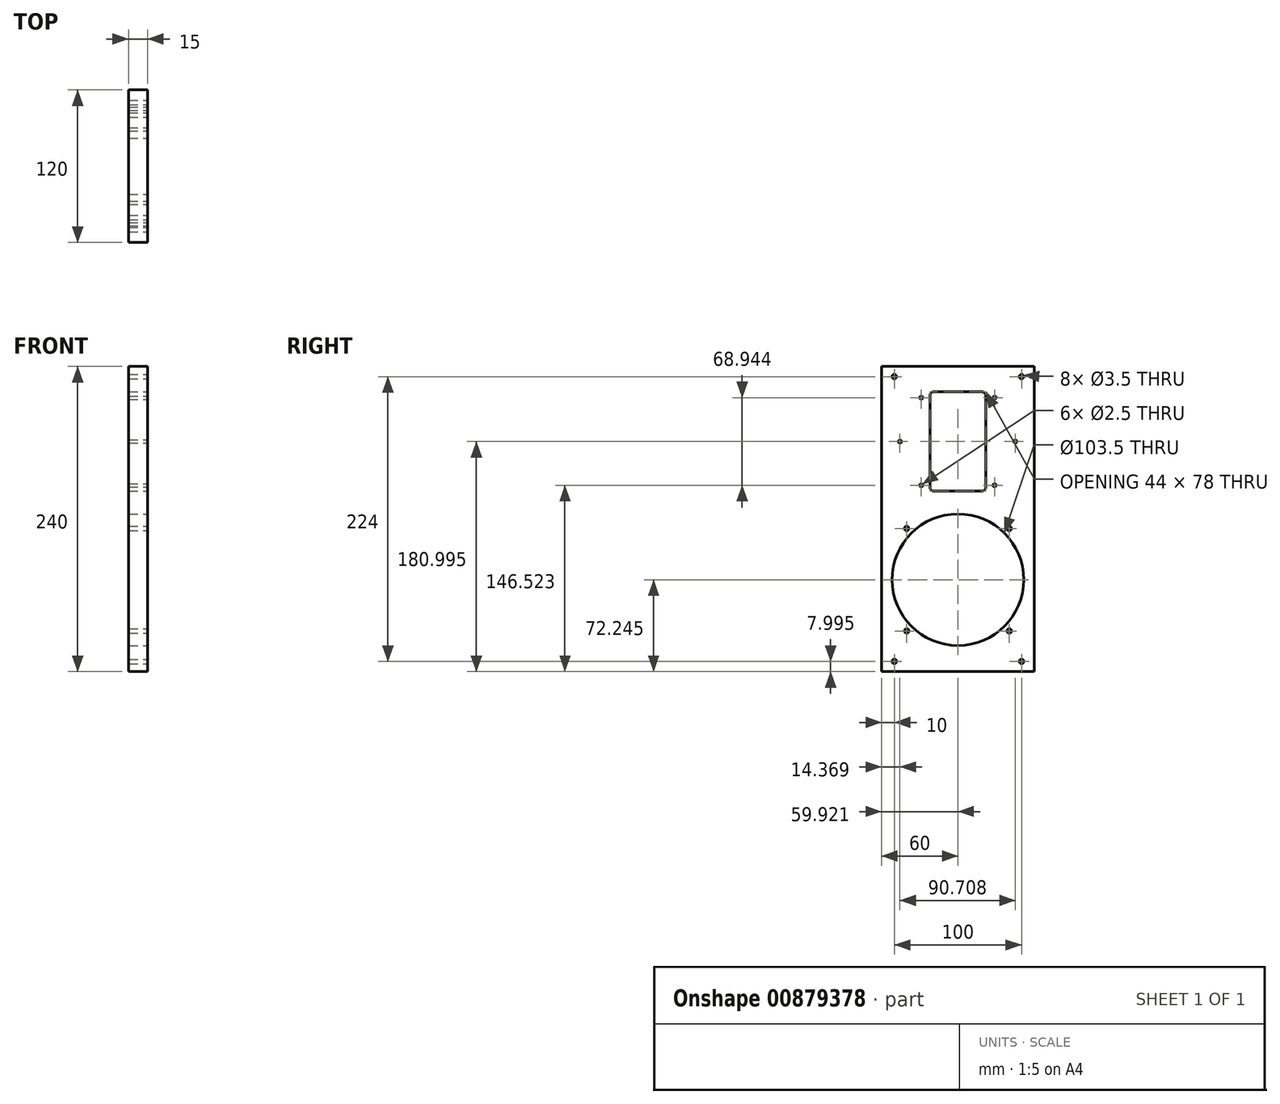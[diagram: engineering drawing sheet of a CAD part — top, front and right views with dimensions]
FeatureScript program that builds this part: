
annotation { "Feature Type Name" : "Feature", "Feature Type Description" : "" }
export const myFeature = defineFeature(function(context is Context, id is Id, definition is map)
    precondition{}
    {
        {
            var Q0;
            Q0=qCreatedBy(makeId("Right.planeOp"),FACE);
            var sketch = newSketch(context, id + "F0", { "sketchPlane" : qUnion([Q0])});
            skLineSegment(sketch, "E0.bottom", {"start": v(60, 124.94) * mm, "end": v(-60, 124.94) * mm});
            skLineSegment(sketch, "E1", {"start": v(60, -115.06) * mm, "end": v(-60, -115.06) * mm});
            skPoint(sketch, "E2", {"position": v(0, -42.81) * mm});
            skCircle(sketch, "E3", {"center": v(0, -42.81) * mm, "radius": 51.75 * mm});
            skCircle(sketch, "E4", {"center": v(40.3, -2.5) * mm, "radius": 1.75 * mm});
            skPoint(sketch, "E5", {"position": v(46.32, 3.5) * mm});
            skPoint(sketch, "E6", {"position": v(47.02, 4.2) * mm});
            skCircle(sketch, "E7.1.0", {"center": v(-40.3, -2.5) * mm, "radius": 1.75 * mm});
            skPoint(sketch, "E7.1.1", {"position": v(-46.32, 3.5) * mm});
            skPoint(sketch, "E7.1.2", {"position": v(-47.02, 4.2) * mm});
            skCircle(sketch, "E7.2.0", {"center": v(-40.3, -83.12) * mm, "radius": 1.75 * mm});
            skPoint(sketch, "E7.2.1", {"position": v(-46.32, -89.13) * mm});
            skPoint(sketch, "E7.2.2", {"position": v(-47.02, -89.84) * mm});
            skCircle(sketch, "E7.3.0", {"center": v(40.3, -83.12) * mm, "radius": 1.75 * mm});
            skPoint(sketch, "E7.3.1", {"position": v(46.32, -89.13) * mm});
            skPoint(sketch, "E7.3.2", {"position": v(47.02, -89.84) * mm});
            skPoint(sketch, "E8.1.0", {"position": v(-57, -42.81) * mm});
            skPoint(sketch, "E8.2.0", {"position": v(0, -99.81) * mm});
            skPoint(sketch, "E8.3.0", {"position": v(57, -42.81) * mm});
            skLineSegment(sketch, "E9.trimOffspring", {"start": v(0, 15.94) * mm, "end": v(0, 15.98) * mm});
            skLineSegment(sketch, "E10.trimOffspring", {"start": v(46.32, 3.5) * mm, "end": v(47.02, 4.2) * mm});
            skPoint(sketch, "E11.start.orphan", {"position": v(0, -109.5) * mm});
            skCircle(sketch, "E12.3.0", {"center": v(28.85, 31.46) * mm, "radius": 1.25 * mm});
            skPoint(sketch, "E13", {"position": v(-0.08, 65.94) * mm});
            skPoint(sketch, "E14", {"position": v(-193.88, 39.27) * mm});
            skLineSegment(sketch, "E15.bottom", {"start": v(-19.08, 104.94) * mm, "end": v(18.92, 104.94) * mm});
            skLineSegment(sketch, "E15.top", {"start": v(-19.08, 26.94) * mm, "end": v(18.92, 26.94) * mm});
            skLineSegment(sketch, "E15.left", {"start": v(-22.08, 101.94) * mm, "end": v(-22.08, 29.94) * mm});
            skLineSegment(sketch, "E15.right", {"start": v(21.92, 101.94) * mm, "end": v(21.92, 29.94) * mm});
            skPoint(sketch, "E16.visualSharp", {"position": v(21.92, 104.94) * mm});
            skArc(sketch, "E16.filletArc", {"start": v(21.92, 101.94) * mm, "mid": v(21.04, 104.06) * mm, "end": v(18.92, 104.94) * mm});
            skPoint(sketch, "E17.visualSharp", {"position": v(-22.08, 104.94) * mm});
            skArc(sketch, "E17.filletArc", {"start": v(-19.08, 104.94) * mm, "mid": v(-21.2, 104.06) * mm, "end": v(-22.08, 101.94) * mm});
            skPoint(sketch, "E18.visualSharp", {"position": v(-22.08, 26.94) * mm});
            skArc(sketch, "E18.filletArc", {"start": v(-22.08, 29.94) * mm, "mid": v(-21.2, 27.81) * mm, "end": v(-19.08, 26.94) * mm});
            skPoint(sketch, "E19.visualSharp", {"position": v(21.92, 26.94) * mm});
            skArc(sketch, "E19.filletArc", {"start": v(18.92, 26.94) * mm, "mid": v(21.04, 27.81) * mm, "end": v(21.92, 29.94) * mm});
            skLineSegment(sketch, "E20", {"start": v(-0.08, 65.94) * mm, "end": v(0, 65.94) * mm});
            skPoint(sketch, "E20.endSnap0", {"position": v(21.92, 65.94) * mm});
            skLineSegment(sketch, "E21", {"start": v(-0.08, 65.94) * mm, "end": v(0, 65.84) * mm});
            skCircle(sketch, "E22.MirrorC", {"center": v(-28.85, 31.46) * mm, "radius": 1.25 * mm});
            skCircle(sketch, "E23.MirrorC", {"center": v(-28.85, 100.4) * mm, "radius": 1.25 * mm});
            skCircle(sketch, "E24.MirrorC", {"center": v(28.85, 100.4) * mm, "radius": 1.25 * mm});
            skCircle(sketch, "E25.3.0", {"center": v(45.08, 65.87) * mm, "radius": 1.25 * mm});
            skCircle(sketch, "E26.3.0", {"center": v(-45.63, 65.87) * mm, "radius": 1.25 * mm});
            skPoint(sketch, "E27.trimOffspring.end.orphan", {"position": v(44.92, 65.94) * mm});
            skLineSegment(sketch, "E28", {"start": v(60, 124.94) * mm, "end": v(60, -115.06) * mm});
            skLineSegment(sketch, "E29", {"start": v(-60, 124.94) * mm, "end": v(-60, -115.06) * mm});
            skPoint(sketch, "E0.left.start.orphan", {"position": v(67.5, 124.94) * mm});
            skPoint(sketch, "E0.right.start.orphan", {"position": v(-67.5, 124.94) * mm});
            skPoint(sketch, "E30.orphan", {"position": v(0, 124.94) * mm});
            skLineSegment(sketch, "E31.trimOffspring", {"start": v(0, 65.84) * mm, "end": v(0, 65.94) * mm});
            skPoint(sketch, "E32.orphan", {"position": v(67.5, -115.06) * mm});
            skLineSegment(sketch, "E33.bottom", {"start": v(-60, 124.94) * mm, "end": v(60, 124.94) * mm});
            skLineSegment(sketch, "E33.top", {"start": v(-60, -115.06) * mm, "end": v(60, -115.06) * mm});
            skPoint(sketch, "E34.right.start.orphan", {"position": v(80.87, 124.94) * mm});
            skPoint(sketch, "E35.trimOffspring.end.orphan", {"position": v(0, -115.06) * mm});
            skCircle(sketch, "E36.0.1.0", {"center": v(-50, 116.94) * mm, "radius": 1.75 * mm});
            skCircle(sketch, "E37.0.1.0", {"center": v(50, 116.94) * mm, "radius": 1.75 * mm});
            skCircle(sketch, "E38.0.1.0", {"center": v(50, -107.06) * mm, "radius": 1.75 * mm});
            skCircle(sketch, "E39.0.1.0", {"center": v(-50, -107.06) * mm, "radius": 1.75 * mm});
            skSolve(sketch);
        }
        {
            var Q0;
            {var subQ4=sQuery(id+"F0.wireOp",EDGE,"E0.left");Q0=makeQuery(id+"F0.imprint","IMPRINT",FACE,{"disambiguationData":[TD([[makeQuery(id+"F0.imprint","IMPRINT",EDGE,{"derivedFrom":subQ4}),-1.0]])]});}
            var Q1;
            Q1=makeQuery(id+"F0.imprint","IMPRINT",FACE,{"disambiguationData":[TD([[makeQuery(id+"F0.imprint","IMPRINT",EDGE,{"derivedFrom":sQuery(id+"F0.wireOp",EDGE,"E15.left")}),-1.0]])]});
            var Q2;
            Q2=makeQuery(id+"F0.imprint","IMPRINT",FACE,{"disambiguationData":[TD([[makeQuery(id+"F0.imprint","IMPRINT",EDGE,{"derivedFrom":sQuery(id+"F0.wireOp",EDGE,"E12.3.0")}),-1.0]])]});
            var Q3;
            Q3=makeQuery(id+"F0.imprint","IMPRINT",FACE,{"disambiguationData":[TD([[makeQuery(id+"F0.imprint","IMPRINT",EDGE,{"derivedFrom":sQuery(id+"F0.wireOp",EDGE,"E3")}),-1.0]])]});
            var Q4;
            Q4=makeQuery(id+"F0.imprint","IMPRINT",FACE,{"disambiguationData":[TD([[makeQuery(id+"F0.imprint","IMPRINT",EDGE,{"derivedFrom":sQuery(id+"F0.wireOp",EDGE,"V4YwmmCf-YE9p-tlqJ-ej81-S3nwM0m2cEtm")}),-1.0]])]});
            extrude(context, id + "F1", {"entities" : qUnion([Q0, Q1, Q2, Q3, Q4]), "oppositeDirection" : true, "depth" : 15 * mm, "offsetDistance" : 25 * mm});
        }
    });
